# Revit family: IAQBOX-D_double_spigot2
name_source: partatom
category: Duct Accessories
revit_build: Autodesk Revit 2015 (Build: 20140606_1530(x64)
units: mm (PartAtom-declared; Revit-internal decimal feet)

## types (3) — shared parameters
Catalogue Pages = http://www.nuaire.info
Classification.Uniclass.Pr.Description = Fans
Classification.Uniclass.Pr.Number = Pr_65_67_29
Duct Connection Height = 90 mm  [stored 0.295276 ft]
Duct Connection Width = 220 mm  [stored 0.721785 ft]
Fax Number = +44(0)2920-858-222
Height = 152 mm
I&M Manual = http://nuaire.info
IFCExportAs = IfcFanType
Length = 858 mm
Manufacturer = Nuaire
Manufacturer Name = Nuaire
Maximum Ambient Temperature = 40 °C
OmniClass Number = 23-33 31 19
OmniClass Title = Fans
Postcode = CF83 1NA
Telephone Number = +44(0)2920-858-200
Type Comments = 1
URL = http://www.nuaire.co.uk
VAT Registration Number = 877308
Warranty Period = 5 Years
Weatherproof or Internal Only = Internal
Weight = 15.80 kg
Width = 645 mm

## per-type parameters (varying)
| type | Description | Pre-Filter Grade | Unit Description |
| IAQBOX-D | Indoor Air Quality Box, Double Width | None | Indoor Air Quality Box, Double Width |
| IAQBOX-D-PM10 | Indoor Air Quality Box, Double Width with pre-Filter | PM10 (G4) | Indoor Air Quality Box, Double Width with pre-Filter |
| IAQBOX-D-PM2.5 | Indoor Air Quality Box, Double Width with pre-Filter | PM2.5 (F7) | Indoor Air Quality Box, Double Width with pre-Filter |

note: column(s) folded — value = type name in every type: Model, Nuaire Model No, Supplier Part No

note: [stored X ft] marks values corroborated as IEEE doubles in the binary element streams (Revit-internal decimal feet)

## geometry (parser evidence)
native form markers: Blend x4, Sweep x15
no freeform markers — native parametric forms only
